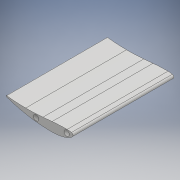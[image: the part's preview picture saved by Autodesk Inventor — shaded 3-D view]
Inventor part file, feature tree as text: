
AUTODESK INVENTOR PART (.ipt)
format: ipt  version: 2018 (Build 220112000, 112)  size: 307,712 bytes
history: native  units: mm
features: other x6, extrude x4, sketch x4, reference x4, projected_geometry x2
ambient origin geometry x8: Origin, YZ Plane, XZ Plane, XY Plane, X Axis, Y Axis, Z Axis, Center Point
bodies: Body1 (feature_tree)
feature tree (20):
  extrude  "押し出し1"  Depth=250.0mm TaperAngle=0.0deg
  other  "作業平面1"
  extrude  "押し出し4"  Depth=225.0mm TaperAngle=0.0deg
  extrude  "押し出し5"  Depth=10.0mm TaperAngle=0.0deg
  extrude  "押し出し6"  Depth=10.0mm TaperAngle=0.0deg
  sketch  "スケッチ1"
  projected_geometry  "投影ループ1"
  sketch  "スケッチ4"
  reference  "参照3"
  reference  "参照4"
  sketch  "スケッチ5"
  projected_geometry  "投影ループ2"
  sketch  "スケッチ6"
  reference  "参照5"
  reference  "参照6"
  other  "<userpath>\Documents\Inventor\Aero\KS-15\Fr.wing\Fr.wing_assy.iam"
  other  "Fr.wing_assy.iam"
  other  "endplate_ver2:2"
  other  "Part1:1"
  other  "newsubflap_top1:1"
